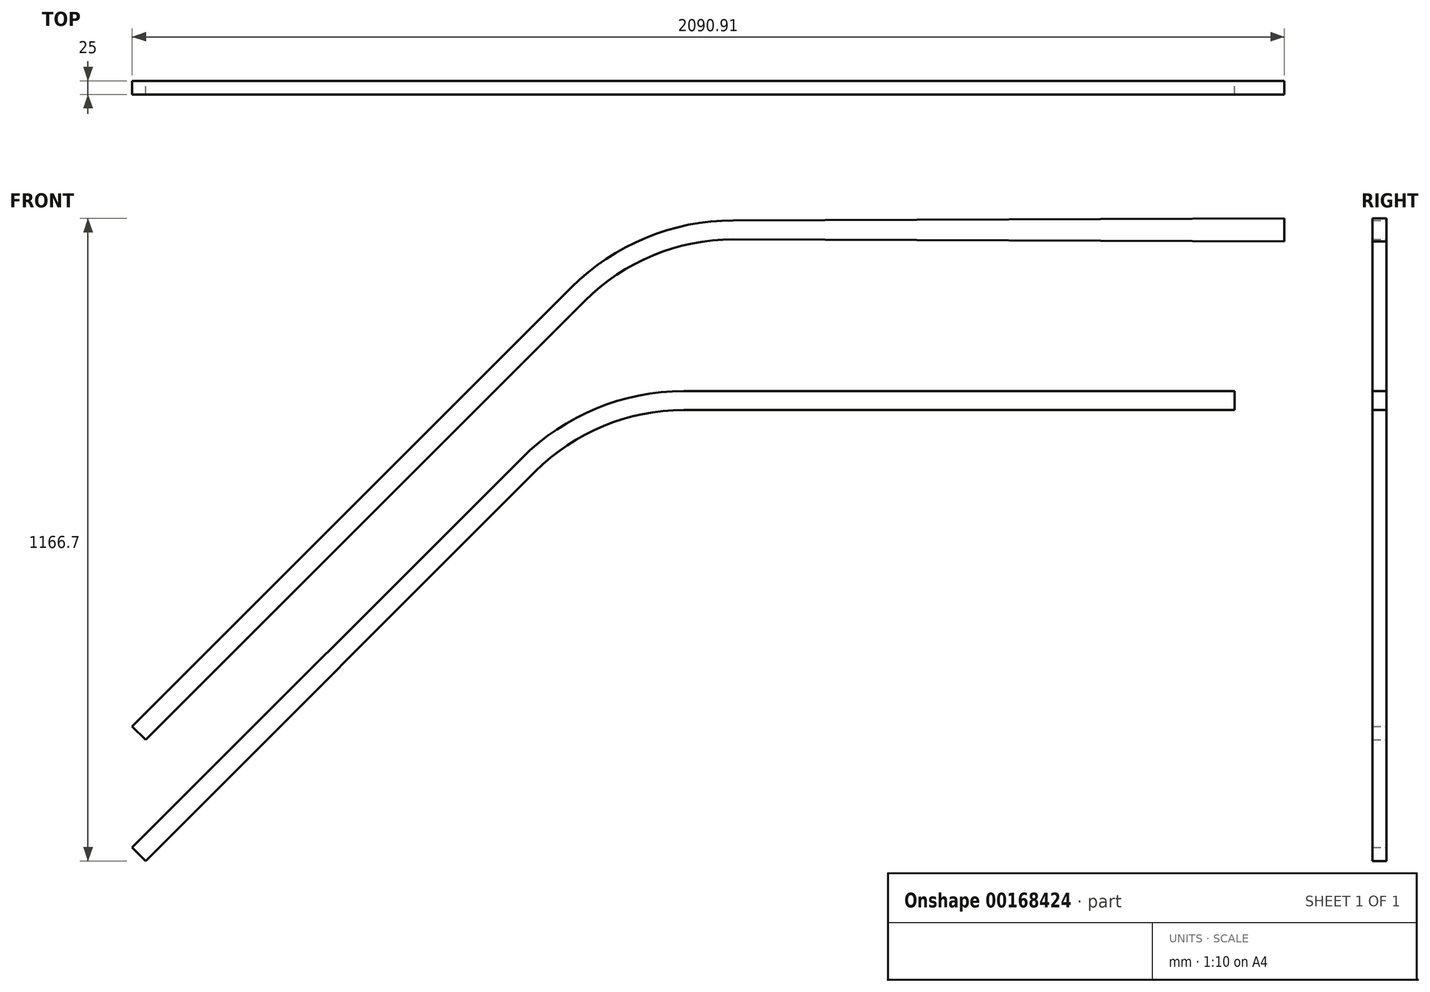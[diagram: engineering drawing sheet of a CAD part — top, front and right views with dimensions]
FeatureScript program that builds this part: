
annotation { "Feature Type Name" : "Feature", "Feature Type Description" : "" }
export const myFeature = defineFeature(function(context is Context, id is Id, definition is map)
    precondition{}
    {
        {
            var Q0;
            Q0=qCreatedBy(makeId("Front.planeOp"),FACE);
            var sketch = newSketch(context, id + "F0", { "sketchPlane" : qUnion([Q0])});
            skLineSegment(sketch, "E0", {"start": v(0, 0) * mm, "end": v(707.1, 707.1) * mm, "construction": true});
            skLineSegment(sketch, "E1", {"start": v(0, 0) * mm, "end": v(0, 220) * mm, "construction": true});
            skLineSegment(sketch, "E2", {"start": v(0, 220) * mm, "end": v(707.1, 927.1) * mm, "construction": true});
            skLineSegment(sketch, "E3", {"start": v(707.1, 927.1) * mm, "end": v(707.1, 707.1) * mm, "construction": true});
            skLineSegment(sketch, "E4", {"start": v(707.1, 927.1) * mm, "end": v(693.67, 940.54) * mm});
            skLineSegment(sketch, "E5", {"start": v(0, 220) * mm, "end": v(-13.44, 233.44) * mm});
            skLineSegment(sketch, "E6", {"start": v(-13.44, 233.44) * mm, "end": v(783.67, 1030.54) * mm});
            skLineSegment(sketch, "E7", {"start": v(786.15, 1028.07) * mm, "end": v(-10.96, 230.96) * mm});
            skLineSegment(sketch, "E8", {"start": v(0, 0) * mm, "end": v(-13.44, 13.44) * mm});
            skLineSegment(sketch, "E9", {"start": v(707.1, 707.1) * mm, "end": v(693.67, 720.54) * mm});
            skLineSegment(sketch, "E10", {"start": v(693.67, 720.54) * mm, "end": v(-13.44, 13.44) * mm});
            skPoint(sketch, "E11", {"position": v(-10.96, 10.96) * mm});
            skPoint(sketch, "E12", {"position": v(696.15, 718.07) * mm});
            skLineSegment(sketch, "E13", {"start": v(696.15, 718.07) * mm, "end": v(-10.96, 10.96) * mm});
            skLineSegment(sketch, "E14", {"start": v(0, 0) * mm, "end": v(707.1, 0) * mm, "construction": true});
            skArc(sketch, "E15", {"start": v(989.95, 824.26) * mm, "mid": v(836.88, 793.82) * mm, "end": v(707.1, 707.1) * mm, "construction": true});
            skLineSegment(sketch, "E16", {"start": v(989.95, 824.26) * mm, "end": v(1989.95, 824.26) * mm, "construction": true});
            skLineSegment(sketch, "E17", {"start": v(707.1, 927.1) * mm, "end": v(797.1, 1017.1) * mm, "construction": true});
            skArc(sketch, "E18", {"start": v(1079.95, 1134.26) * mm, "mid": v(926.88, 1103.82) * mm, "end": v(797.1, 1017.1) * mm, "construction": true});
            skLineSegment(sketch, "E19", {"start": v(1079.95, 1134.26) * mm, "end": v(2079.95, 1134.26) * mm, "construction": true});
            skArc(sketch, "E20.trimOffspring", {"start": v(680.83, 707.7) * mm, "mid": v(681.84, 695.44) * mm, "end": v(683.22, 683.22) * mm, "construction": true});
            skLineSegment(sketch, "E21", {"start": v(797.1, 1017.1) * mm, "end": v(783.67, 1030.54) * mm});
            skArc(sketch, "E22.0", {"start": v(1079.95, 1153.26) * mm, "mid": v(919.6, 1121.37) * mm, "end": v(783.67, 1030.54) * mm});
            skArc(sketch, "E23.0", {"start": v(1079.95, 1149.76) * mm, "mid": v(920.94, 1118.14) * mm, "end": v(786.15, 1028.07) * mm});
            skLineSegment(sketch, "E24", {"start": v(1079.95, 1153.26) * mm, "end": v(1079.95, 1134.26) * mm});
            skLineSegment(sketch, "E25", {"start": v(1079.95, 1149.76) * mm, "end": v(2079.95, 1153.26) * mm});
            skLineSegment(sketch, "E26", {"start": v(1079.95, 1153.26) * mm, "end": v(2079.95, 1156.76) * mm});
            skLineSegment(sketch, "E27", {"start": v(2079.95, 1156.76) * mm, "end": v(2079.95, 1134.26) * mm});
            skArc(sketch, "E28.0", {"start": v(989.95, 843.26) * mm, "mid": v(829.6, 811.37) * mm, "end": v(693.67, 720.54) * mm});
            skArc(sketch, "E29.0", {"start": v(989.95, 839.76) * mm, "mid": v(830.94, 808.14) * mm, "end": v(696.15, 718.07) * mm});
            skLineSegment(sketch, "E30", {"start": v(989.95, 843.26) * mm, "end": v(989.95, 824.26) * mm});
            skLineSegment(sketch, "E31", {"start": v(989.95, 839.76) * mm, "end": v(1989.95, 839.76) * mm});
            skLineSegment(sketch, "E32", {"start": v(989.95, 843.26) * mm, "end": v(1989.95, 843.26) * mm});
            skLineSegment(sketch, "E33", {"start": v(1989.95, 843.26) * mm, "end": v(1989.95, 824.26) * mm});
            skLineSegment(sketch, "E34.MirrorCS", {"start": v(0, 220) * mm, "end": v(13.44, 206.56) * mm});
            skLineSegment(sketch, "E35.MirrorCS", {"start": v(13.44, 206.56) * mm, "end": v(810.54, 1003.67) * mm});
            skLineSegment(sketch, "E36.MirrorCS", {"start": v(1079.95, 1115.26) * mm, "end": v(2079.95, 1111.76) * mm});
            skLineSegment(sketch, "E37.MirrorCS", {"start": v(2079.95, 1111.76) * mm, "end": v(2079.95, 1134.26) * mm});
            skLineSegment(sketch, "E38.MirrorCS", {"start": v(1989.95, 805.26) * mm, "end": v(1989.95, 824.26) * mm});
            skLineSegment(sketch, "E39.MirrorCS", {"start": v(989.95, 805.26) * mm, "end": v(1989.95, 805.26) * mm});
            skLineSegment(sketch, "E40.MirrorCS", {"start": v(0, 0) * mm, "end": v(13.44, -13.44) * mm});
            skLineSegment(sketch, "E41.MirrorCS", {"start": v(720.54, 693.67) * mm, "end": v(13.44, -13.44) * mm});
            skArc(sketch, "E42.0", {"start": v(1079.95, 1115.26) * mm, "mid": v(934.15, 1086.26) * mm, "end": v(810.54, 1003.67) * mm});
            skArc(sketch, "E43.0", {"start": v(989.95, 805.26) * mm, "mid": v(844.15, 776.26) * mm, "end": v(720.54, 693.67) * mm});
            skSolve(sketch);
        }
        {
            var Q0;
            {var subQ7=sQuery(id+"F0.wireOp",EDGE,"E23.0");Q0=makeQuery(id+"F0.imprint","IMPRINT",FACE,{"disambiguationData":[TD([[makeQuery(id+"F0.imprint","IMPRINT",EDGE,{"derivedFrom":subQ7}),1.0]])]});}
            var Q1;
            {var subQ2=sQuery(id+"F0.wireOp",EDGE,"E13");Q1=makeQuery(id+"F0.imprint","IMPRINT",FACE,{"disambiguationData":[TD([[makeQuery(id+"F0.imprint","IMPRINT",EDGE,{"derivedFrom":subQ2}),1.0]])]});}
            extrude(context, id + "F1", {"entities" : qUnion([Q0, Q1]), "depth" : 25 * mm});
        }
    });
